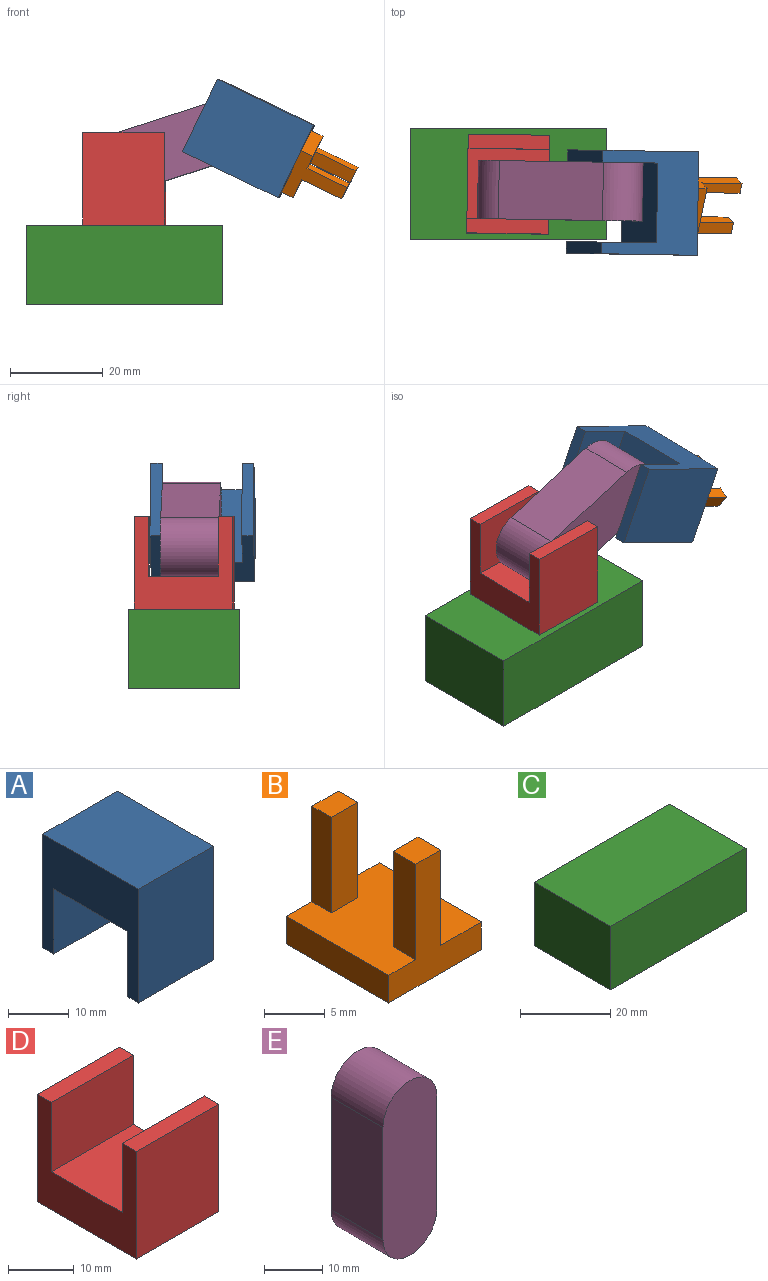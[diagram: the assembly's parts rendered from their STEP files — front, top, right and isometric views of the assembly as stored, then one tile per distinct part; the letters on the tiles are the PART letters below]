
ASSEMBLY  parts=5 mates=4
PART A: 10 faces, bbox 17.4x22.4x23 mm
  f0: plane 17.42x17.28mm, normal (0,0,-1), area 301mm2, adj f1,f3,f6,f8
  f1: plane 23x22.35mm, normal (-1,0,0), area 285.8mm2, adj f0,f2,f4,f5,f6,f7,f8,f9
  f2: plane 22.35x17.42mm, normal (0,0,1), area 389.3mm2, adj f1,f3,f4,f5
  f3: plane 23x22.35mm, normal (1,0,0), area 285.8mm2, adj f0,f2,f4,f5,f6,f7,f8,f9
  f4: plane 23x17.42mm, normal (0,-1,0), area 400.6mm2, adj f1,f2,f3,f7
  f5: plane 23x17.42mm, normal (0,1,0), area 400.6mm2, adj f1,f2,f3,f9
  f6: plane 17.42x13.21mm, normal (0,1,0), area 230.1mm2, adj f0,f1,f3,f7
  f7: plane 17.42x2.52mm, normal (0,0,-1), area 43.9mm2, adj f1,f3,f4,f6
  f8: plane 17.42x13.21mm, normal (0,-1,0), area 230.1mm2, adj f0,f1,f3,f9
  f9: plane 17.42x2.56mm, normal (0,0,-1), area 44.5mm2, adj f1,f3,f5,f8
PART B: 14 faces, bbox 10.8x11.9x12.4 mm
  f0: plane 11.94x2.8mm, normal (-1,0,0), area 33.4mm2, adj f1,f3,f4,f5
  f1: plane 11.94x10.82mm, normal (0,0,1), area 114.5mm2, adj f0,f2,f4,f5,f6,f7,f8,f10
  f2: plane 11.94x2.8mm, normal (1,0,0), area 33.4mm2, adj f1,f3,f4,f5
  f3: plane 11.94x10.82mm, normal (0,0,-1), area 129.1mm2, adj f0,f2,f4,f5
  f4: plane 12.45x10.82mm, normal (0,1,0), area 60mm2, adj f0,f1,f2,f3,f10,f12,f13
  f5: plane 12.45x10.82mm, normal (0,-1,0), area 58.2mm2, adj f0,f1,f2,f3,f6,f7,f9
  f6: plane 9.65x2.63mm, normal (-1,0,0), area 25.3mm2, adj f1,f5,f8,f9
  f7: plane 9.65x2.63mm, normal (1,0,0), area 25.3mm2, adj f1,f5,f8,f9
  f8: plane 9.65x2.89mm, normal (0,1,0), area 27.9mm2, adj f1,f6,f7,f9
  f9: plane 2.89x2.63mm, normal (0,0,1), area 7.6mm2, adj f5,f6,f7,f8
  f10: plane 9.65x2.28mm, normal (-1,0,0), area 22mm2, adj f1,f4,f11,f13
  f11: plane 9.65x3.08mm, normal (0,-1,0), area 29.8mm2, adj f1,f10,f12,f13
  f12: plane 9.65x2.28mm, normal (1,0,0), area 22mm2, adj f1,f4,f11,f13
  f13: plane 3.08x2.28mm, normal (0,0,1), area 7mm2, adj f4,f10,f11,f12
PART C: 6 faces, bbox 42.5x24x17.3 mm
  f0: plane 24x17.27mm, normal (-1,0,0), area 414.5mm2, adj f1,f3,f4,f5
  f1: plane 42.49x17.27mm, normal (0,-1,0), area 733.8mm2, adj f0,f2,f4,f5
  f2: plane 24x17.27mm, normal (1,0,0), area 414.5mm2, adj f1,f3,f4,f5
  f3: plane 42.49x17.27mm, normal (0,1,0), area 733.8mm2, adj f0,f2,f4,f5
  f4: plane 42.49x24mm, normal (0,0,1), area 1019.6mm2, adj f0,f1,f2,f3
  f5: plane 42.49x24mm, normal (0,0,-1), area 1019.6mm2, adj f0,f1,f2,f3
PART D: 10 faces, bbox 17.7x21.4x20 mm
  f0: plane 17.66x15.19mm, normal (0,0,1), area 268.2mm2, adj f1,f3,f6,f8
  f1: plane 21.36x20.02mm, normal (-1,0,0), area 231.7mm2, adj f0,f2,f4,f5,f6,f7,f8,f9
  f2: plane 20.02x17.66mm, normal (0,-1,0), area 353.5mm2, adj f1,f3,f5,f7
  f3: plane 21.36x20.02mm, normal (1,0,0), area 231.7mm2, adj f0,f2,f4,f5,f6,f7,f8,f9
  f4: plane 20.02x17.66mm, normal (0,1,0), area 353.5mm2, adj f1,f3,f5,f9
  f5: plane 21.36x17.66mm, normal (0,0,-1), area 377.3mm2, adj f1,f2,f3,f4
  f6: plane 17.66x12.9mm, normal (0,1,0), area 227.9mm2, adj f0,f1,f3,f7
  f7: plane 17.66x3.12mm, normal (0,0,1), area 55.2mm2, adj f1,f2,f3,f6
  f8: plane 17.66x12.9mm, normal (0,-1,0), area 227.9mm2, adj f0,f1,f3,f9
  f9: plane 17.66x3.06mm, normal (0,0,1), area 53.9mm2, adj f1,f3,f4,f8
PART E: 6 faces, bbox 13.1x12.6x36.8 mm
  f0: plane 23.65x12.6mm, normal (1,0,0), area 298mm2, adj f1,f3,f4,f5
  f1: cylinder r=6.56mm len=13.11mm, axis (0,-1,0), area 259.5mm2, adj f0,f2,f4,f5
  f2: plane 23.65x12.6mm, normal (-1,0,0), area 298mm2, adj f1,f3,f4,f5
  f3: cylinder r=6.56mm len=13.11mm, axis (0,-1,0), area 259.5mm2, adj f0,f2,f4,f5
  f4: plane 36.77x13.11mm, normal (0,1,0), area 445.2mm2, adj f0,f1,f2,f3
  f5: plane 36.77x13.11mm, normal (0,-1,0), area 445.2mm2, adj f0,f1,f2,f3
PLACE A rot(axis=(0.01,1,0),115.7deg) t=(-62.49,-3.47,81.96)mm
PLACE B rot(axis=(0.21,0.97,0.12),117.1deg) t=(-64.08,-10.97,75.62)mm
PLACE C t=(-51.22,-0.4,-5.8)mm fixed
PLACE D rot(axis=(0,0,-1),0.9deg) t=(-51.4,-0.07,-5.8)mm
PLACE E rot(axis=(0.01,1,-0.01),72.1deg) t=(-79.89,-0.88,30.97)mm
MATE revolute E.f3 <-> A.f8  axis (0.02,1,0) through (-7.39,16.28,32.32)mm
MATE revolute D.f5 <-> C.f4  axis (0,0,-1) through (-29.98,11.6,11.47)mm
MATE revolute D.f6 <-> E.f1  axis (0.02,1,0) through (-30.09,4.04,25.04)mm
MATE revolute B.f3 <-> A.f2  axis (-0.9,0.01,0.43) through (7.24,7.43,25.2)mm
